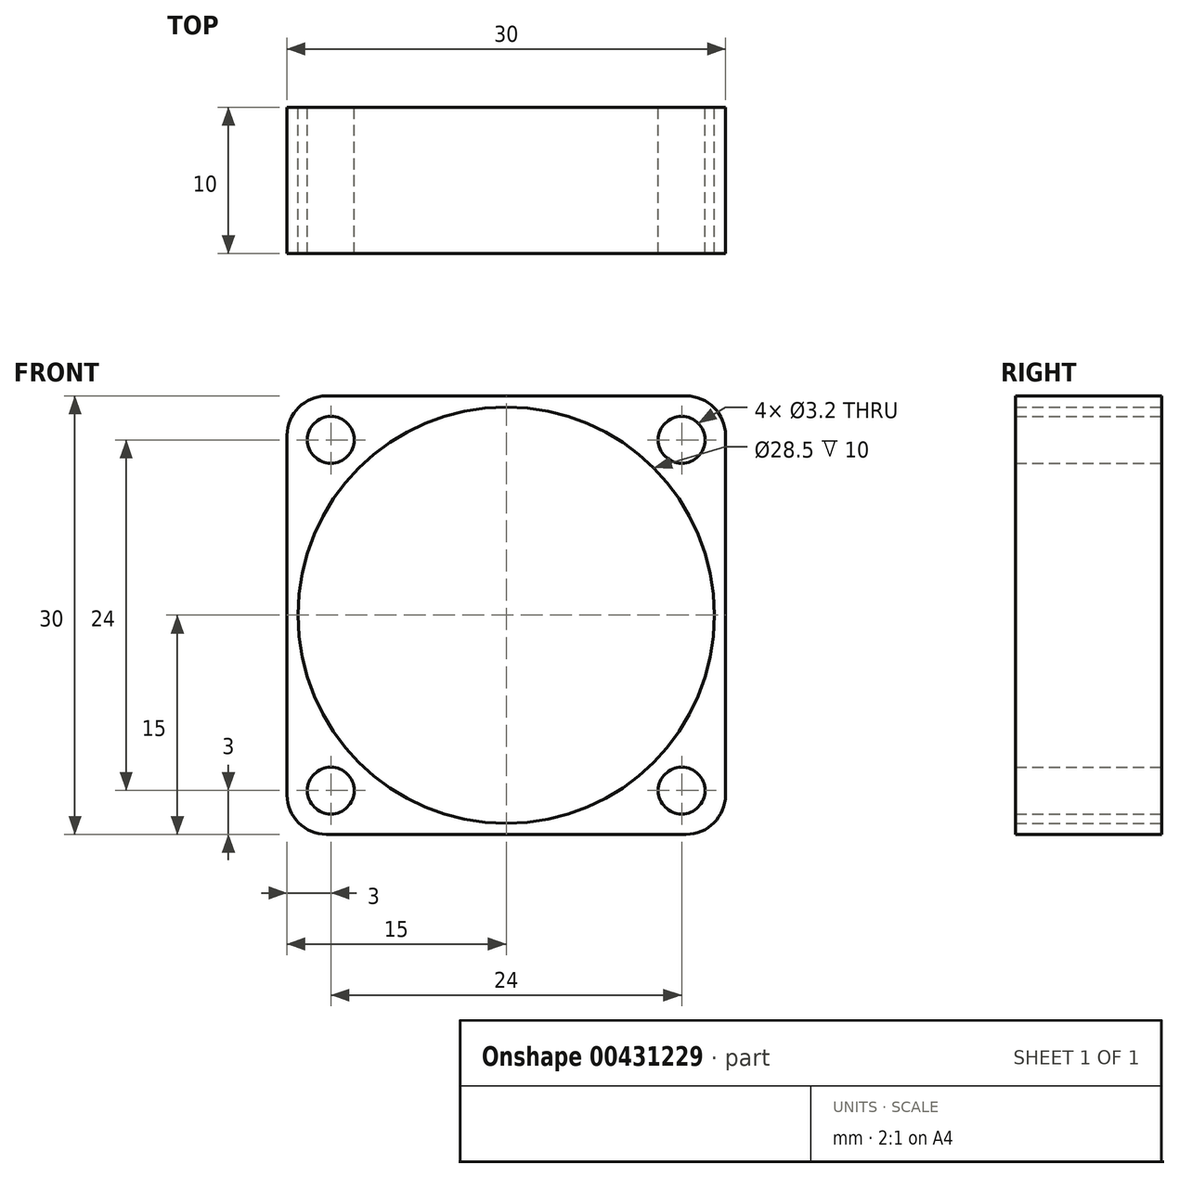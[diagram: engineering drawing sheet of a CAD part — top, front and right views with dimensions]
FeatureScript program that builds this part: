
annotation { "Feature Type Name" : "Feature", "Feature Type Description" : "" }
export const myFeature = defineFeature(function(context is Context, id is Id, definition is map)
    precondition{}
    {
        {
            var Q0;
            Q0=qCreatedBy(makeId("Front.planeOp"),FACE);
            var sketch = newSketch(context, id + "F0", { "sketchPlane" : qUnion([Q0])});
            skLineSegment(sketch, "E0", {"start": v(0, 15) * mm, "end": v(-12.3, 15) * mm});
            skLineSegment(sketch, "E1", {"start": v(-15, 12.3) * mm, "end": v(-15, 0) * mm});
            skCircle(sketch, "E2", {"center": v(-12, 12) * mm, "radius": 1.6 * mm});
            skPoint(sketch, "E3.visualSharp", {"position": v(-15, 15) * mm});
            skArc(sketch, "E3.filletArc", {"start": v(-12.3, 15) * mm, "mid": v(-14.2, 14.2) * mm, "end": v(-15, 12.3) * mm});
            skCircle(sketch, "E4.MirrorC", {"center": v(12, 12) * mm, "radius": 1.6 * mm});
            skArc(sketch, "E5.MirrorCS", {"start": v(12.3, 15) * mm, "mid": v(14.2, 14.2) * mm, "end": v(15, 12.3) * mm});
            skLineSegment(sketch, "E6.MirrorCS", {"start": v(15, 12.3) * mm, "end": v(15, 0) * mm});
            skPoint(sketch, "E7.MirrorP", {"position": v(15, 15) * mm});
            skLineSegment(sketch, "E8.MirrorCS", {"start": v(0, 15) * mm, "end": v(12.3, 15) * mm});
            skLineSegment(sketch, "E9.MirrorCS", {"start": v(15, -12.3) * mm, "end": v(15, 0) * mm});
            skLineSegment(sketch, "E10.MirrorCS", {"start": v(0, -15) * mm, "end": v(12.3, -15) * mm});
            skArc(sketch, "E11.MirrorCS", {"start": v(12.3, -15) * mm, "mid": v(14.2, -14.2) * mm, "end": v(15, -12.3) * mm});
            skLineSegment(sketch, "E12.MirrorCS", {"start": v(0, -15) * mm, "end": v(-12.3, -15) * mm});
            skLineSegment(sketch, "E13.MirrorCS", {"start": v(-15, -12.3) * mm, "end": v(-15, 0) * mm});
            skPoint(sketch, "E14.MirrorP", {"position": v(-15, -15) * mm});
            skCircle(sketch, "E15.MirrorC", {"center": v(-12, -12) * mm, "radius": 1.6 * mm});
            skPoint(sketch, "E16.MirrorP", {"position": v(15, -15) * mm});
            skCircle(sketch, "E17.MirrorC", {"center": v(12, -12) * mm, "radius": 1.6 * mm});
            skArc(sketch, "E18.MirrorCS", {"start": v(-12.3, -15) * mm, "mid": v(-14.2, -14.2) * mm, "end": v(-15, -12.3) * mm});
            skCircle(sketch, "E19", {"center": v(0, 0) * mm, "radius": 14.25 * mm});
            skSolve(sketch);
        }
        {
            var Q0;
            Q0 = qSketchRegion(id + "F0", true);
            extrude(context, id + "F1", {"entities" : qUnion([Q0]), "depth" : 10 * mm});
        }
    });
